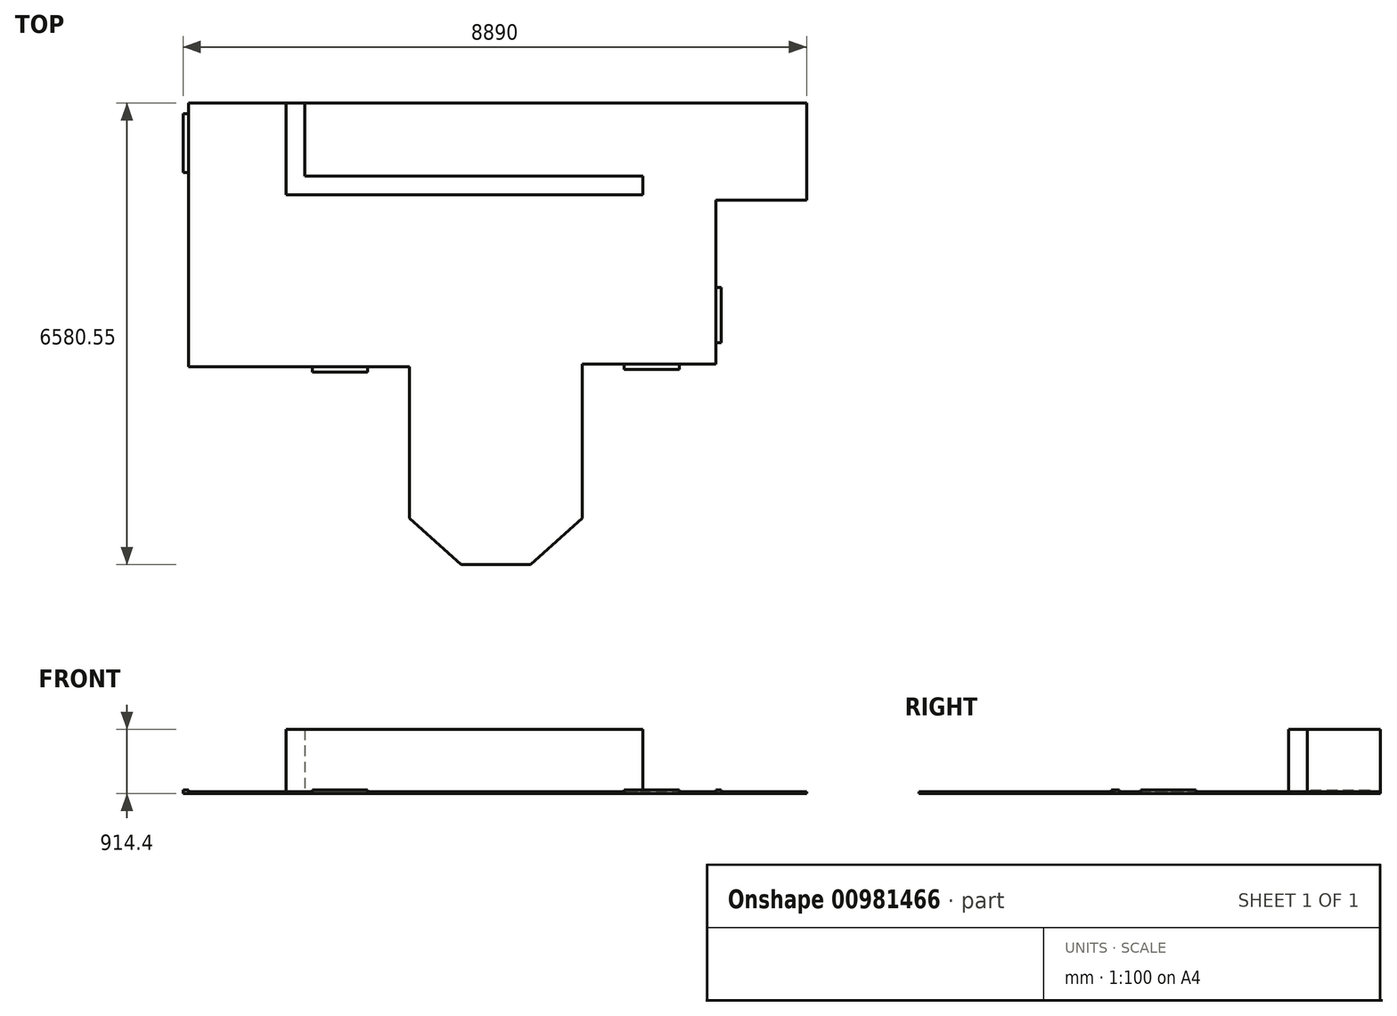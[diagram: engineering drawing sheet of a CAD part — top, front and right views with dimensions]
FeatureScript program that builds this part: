
annotation { "Feature Type Name" : "Feature", "Feature Type Description" : "" }
export const myFeature = defineFeature(function(context is Context, id is Id, definition is map)
    precondition{}
    {
        {
            var Q0;
            Q0=qCreatedBy(makeId("Top.planeOp"),FACE);
            var sketch = newSketch(context, id + "F0", { "sketchPlane" : qUnion([Q0])});
            skLineSegment(sketch, "E0", {"start": v(0, 0) * mm, "end": v(8813.8, 0) * mm});
            skLineSegment(sketch, "E1", {"start": v(0, 0) * mm, "end": v(0, -3759.2) * mm});
            skLineSegment(sketch, "E2", {"start": v(0, -3759.2) * mm, "end": v(3149.6, -3759.2) * mm});
            skLineSegment(sketch, "E3", {"start": v(3149.6, -3759.2) * mm, "end": v(3149.6, -5918.2) * mm});
            skLineSegment(sketch, "E4", {"start": v(3149.6, -5918.2) * mm, "end": v(3886.2, -6580.55) * mm});
            skLineSegment(sketch, "E5", {"start": v(3886.2, -6580.55) * mm, "end": v(4876.8, -6580.55) * mm});
            skLineSegment(sketch, "E6", {"start": v(4876.8, -6580.55) * mm, "end": v(5613.4, -5918.2) * mm});
            skLineSegment(sketch, "E7", {"start": v(5613.4, -5918.2) * mm, "end": v(5613.4, -3721.1) * mm});
            skLineSegment(sketch, "E8", {"start": v(5613.4, -3721.1) * mm, "end": v(7518.4, -3721.1) * mm});
            skLineSegment(sketch, "E9", {"start": v(7518.4, -3721.1) * mm, "end": v(7518.4, -1384.3) * mm});
            skLineSegment(sketch, "E10", {"start": v(7518.4, -1384.3) * mm, "end": v(8813.8, -1384.3) * mm});
            skLineSegment(sketch, "E11", {"start": v(8813.8, -1384.3) * mm, "end": v(8813.8, 0) * mm});
            skSolve(sketch);
        }
        {
            var Q0;
            Q0=qCreatedBy(makeId("Top.planeOp"),FACE);
            var sketch = newSketch(context, id + "F1", { "sketchPlane" : qUnion([Q0])});
            skLineSegment(sketch, "E12", {"start": v(1524, 0) * mm, "end": v(1524, -1174.75) * mm, "construction": true});
            skLineSegment(sketch, "E13", {"start": v(1524, -1174.75) * mm, "end": v(6477, -1174.75) * mm, "construction": true});
            skLineSegment(sketch, "E14", {"start": v(6477, -1174.75) * mm, "end": v(6477, -1308.1) * mm});
            skLineSegment(sketch, "E15", {"start": v(6477, -1308.1) * mm, "end": v(1390.65, -1308.1) * mm});
            skLineSegment(sketch, "E16", {"start": v(1390.65, -1308.1) * mm, "end": v(1390.65, 0) * mm});
            skLineSegment(sketch, "E17", {"start": v(1390.65, 0) * mm, "end": v(1524, 0) * mm});
            skLineSegment(sketch, "E18", {"start": v(6477, -1174.75) * mm, "end": v(6477, -1041.4) * mm});
            skLineSegment(sketch, "E19", {"start": v(6477, -1041.4) * mm, "end": v(1657.35, -1041.4) * mm});
            skLineSegment(sketch, "E20", {"start": v(1657.35, -1041.4) * mm, "end": v(1657.35, 0) * mm});
            skLineSegment(sketch, "E21", {"start": v(1657.35, 0) * mm, "end": v(1524, 0) * mm});
            skSolve(sketch);
        }
        {
            var Q0;
            Q0=qCreatedBy(makeId("Top.planeOp"),FACE);
            var sketch = newSketch(context, id + "F2", { "sketchPlane" : qUnion([Q0])});
            skLineSegment(sketch, "E22.bottom", {"start": v(0, -990.6) * mm, "end": v(-76.2, -990.6) * mm});
            skLineSegment(sketch, "E22.top", {"start": v(0, -152.4) * mm, "end": v(-76.2, -152.4) * mm});
            skLineSegment(sketch, "E22.left", {"start": v(0, -990.6) * mm, "end": v(0, -152.4) * mm});
            skLineSegment(sketch, "E22.right", {"start": v(-76.2, -990.6) * mm, "end": v(-76.2, -152.4) * mm});
            skLineSegment(sketch, "E23.bottom", {"start": v(2552.7, -3759.2) * mm, "end": v(1765.3, -3759.2) * mm});
            skLineSegment(sketch, "E23.top", {"start": v(2552.7, -3835.4) * mm, "end": v(1765.3, -3835.4) * mm});
            skLineSegment(sketch, "E23.left", {"start": v(2552.7, -3759.2) * mm, "end": v(2552.7, -3835.4) * mm});
            skLineSegment(sketch, "E23.right", {"start": v(1765.3, -3759.2) * mm, "end": v(1765.3, -3835.4) * mm});
            skLineSegment(sketch, "E24.bottom", {"start": v(6997.7, -3721.1) * mm, "end": v(6210.3, -3721.1) * mm});
            skLineSegment(sketch, "E24.top", {"start": v(6997.7, -3797.3) * mm, "end": v(6210.3, -3797.3) * mm});
            skLineSegment(sketch, "E24.left", {"start": v(6997.7, -3721.1) * mm, "end": v(6997.7, -3797.3) * mm});
            skLineSegment(sketch, "E24.right", {"start": v(6210.3, -3721.1) * mm, "end": v(6210.3, -3797.3) * mm});
            skLineSegment(sketch, "E25.bottom", {"start": v(7594.6, -3416.3) * mm, "end": v(7518.4, -3416.3) * mm});
            skLineSegment(sketch, "E25.top", {"start": v(7594.6, -2628.9) * mm, "end": v(7518.4, -2628.9) * mm});
            skLineSegment(sketch, "E25.left", {"start": v(7594.6, -3416.3) * mm, "end": v(7594.6, -2628.9) * mm});
            skLineSegment(sketch, "E25.right", {"start": v(7518.4, -3416.3) * mm, "end": v(7518.4, -2628.9) * mm});
            skSolve(sketch);
        }
        {
            var Q0;
            Q0 = qSketchRegion(id + "F0", true);
            extrude(context, id + "F3", {"entities" : qUnion([Q0]), "depth" : 25.4 * mm, "offsetDistance" : 25.4 * mm});
        }
        {
            var Q0;
            Q0 = qSketchRegion(id + "F1", true);
            extrude(context, id + "F4", {"entities" : qUnion([Q0]), "operationType" : NewBodyOperationType.ADD, "depth" : 914.4 * mm, "offsetDistance" : 25.4 * mm});
        }
        {
            var Q0;
            Q0 = qSketchRegion(id + "F2", true);
            extrude(context, id + "F5", {"entities" : qUnion([Q0]), "operationType" : NewBodyOperationType.ADD, "depth" : 50.8 * mm, "offsetDistance" : 25.4 * mm});
        }
    });
